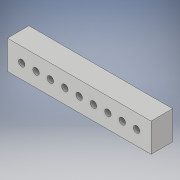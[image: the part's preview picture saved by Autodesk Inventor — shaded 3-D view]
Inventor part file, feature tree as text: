
AUTODESK INVENTOR PART (.ipt)
format: ipt  version: 2018 (Build 220112000, 112)  size: 128,000 bytes
history: native  units: in
note: dims shown in document units (in); Inventor stores cm internally (conversion verified against a paired STEP export)
features: extrude x3, sketch x2, pattern_linear x1
ambient origin geometry x8: Origin, YZ Plane, XZ Plane, XY Plane, X Axis, Y Axis, Z Axis, Center Point
bodies: Solid1 (feature_tree)
feature tree (6):
  sketch  "Sketch1"  dims[d0=0.45in d1=2.0in]
  extrude  "Extrusion1"  Depth=2.0in
  extrude  "Extrusion2"  Depth=1.5in TaperAngle=0.0deg
  pattern_linear  "Rectangular Pattern1"  Spacing1=1.5in  [1 undecoded]
  extrude  "Extrusion3"  Depth=1.0in
  sketch  "Sketch2"  dims[d2=10.0in d3=1.5in d4=0.0in d5=1.5in d6=0.0in d7=3.5433in d9=1.0in d10=0.45in d11=5.5in d12=0.0in]
note: 1 required parameter value undecoded (feature->parameter linkage not recoverable at this tier; creation-order binding heuristic only, values carry confidence <= 0.55)
